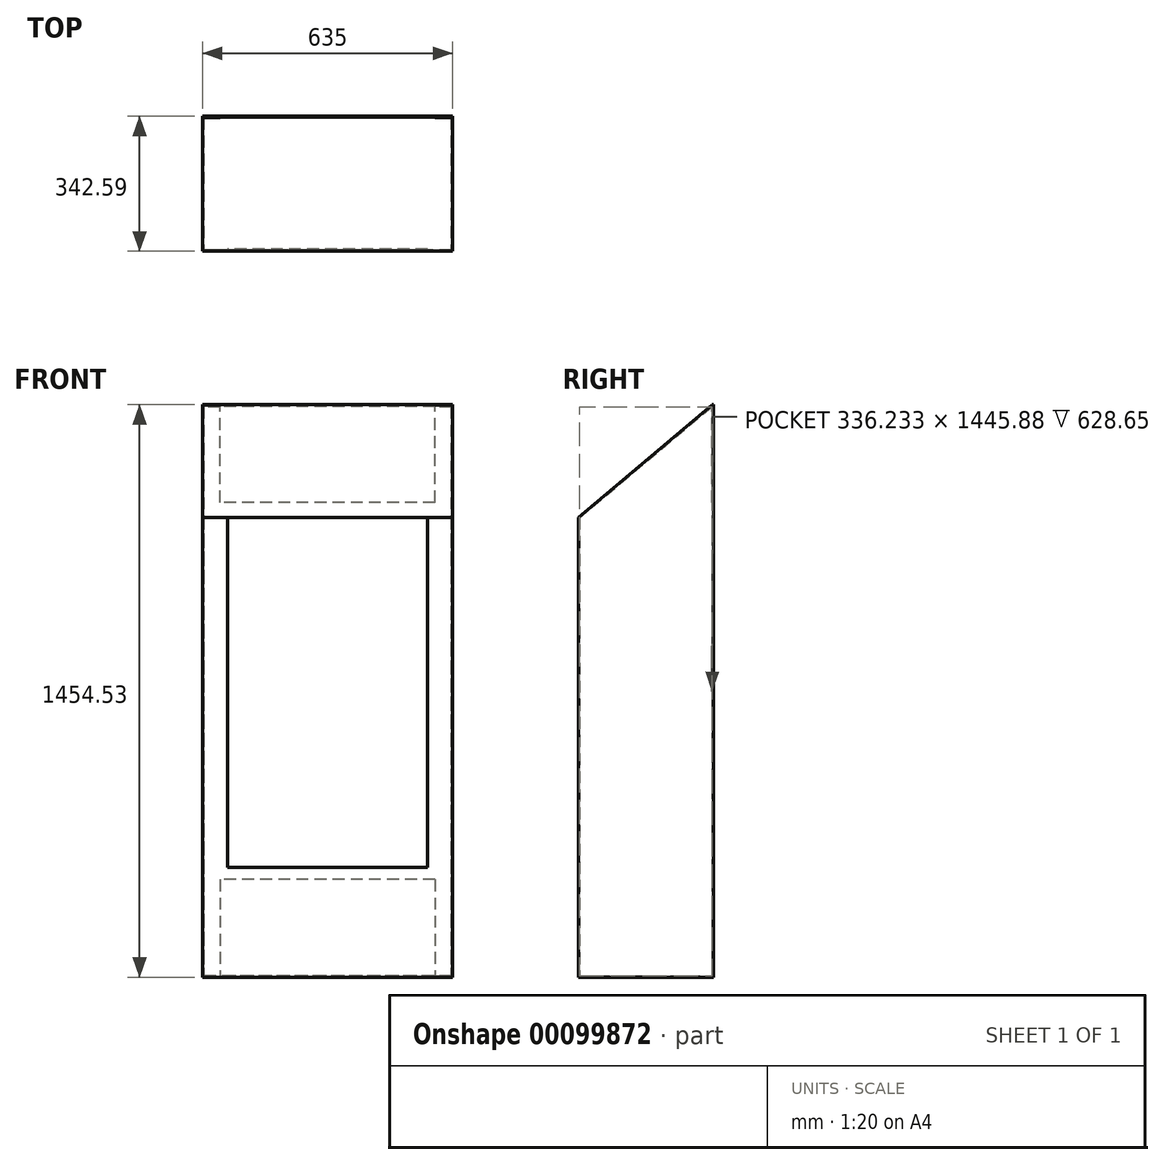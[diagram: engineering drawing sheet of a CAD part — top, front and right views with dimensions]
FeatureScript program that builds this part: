
annotation { "Feature Type Name" : "Feature", "Feature Type Description" : "" }
export const myFeature = defineFeature(function(context is Context, id is Id, definition is map)
    precondition{}
    {
        {
            var Q0;
            Q0=qCreatedBy(makeId("Right.planeOp"),FACE);
            var sketch = newSketch(context, id + "F0", { "sketchPlane" : qUnion([Q0])});
            skLineSegment(sketch, "E0", {"start": v(0, 0) * mm, "end": v(0, 1454.53) * mm});
            skLineSegment(sketch, "E1", {"start": v(0, 1454.53) * mm, "end": v(-341, 1168.4) * mm});
            skLineSegment(sketch, "E2", {"start": v(-341, 1168.4) * mm, "end": v(-341, 0) * mm});
            skLineSegment(sketch, "E3", {"start": v(-341, 0) * mm, "end": v(0, 0) * mm});
            skSolve(sketch);
        }
        {
            var Q0;
            Q0 = qSketchRegion(id + "F0", true);
            extrude(context, id + "F1", {"entities" : qUnion([Q0]), "endBound" : BoundingType.SYMMETRIC, "depth" : 635 * mm});
        }
        {
            var Q0;
            Q0=makeQuery(id+"F1.opExtrude","SWEPT_FACE",FACE,{"disambiguationData":[OSD([sQuery(id+"F0.wireOp",EDGE,"E0")])]});
            shell(context, id + "F2", {"entities" : qUnion([Q0]), "thickness" : 3.17 * mm});
        }
        {
            var Q0;
            Q0=qCreatedBy(makeId("Front.planeOp"),FACE);
            var sketch = newSketch(context, id + "F3", { "sketchPlane" : qUnion([Q0])});
            skLineSegment(sketch, "E4.bottom", {"start": v(273.11, 247.9) * mm, "end": v(-273.11, 247.9) * mm});
            skLineSegment(sketch, "E4.top", {"start": v(273.11, 1206.62) * mm, "end": v(-273.11, 1206.62) * mm});
            skLineSegment(sketch, "E4.left", {"start": v(317.5, 247.9) * mm, "end": v(317.5, 1206.62) * mm});
            skLineSegment(sketch, "E4.right", {"start": v(-317.5, 247.9) * mm, "end": v(-317.5, 1206.62) * mm});
            skLineSegment(sketch, "E5.top", {"start": v(317.5, 1454.53) * mm, "end": v(273.11, 1454.53) * mm});
            skLineSegment(sketch, "E5.left", {"start": v(317.5, 1206.62) * mm, "end": v(317.5, 1454.53) * mm});
            skLineSegment(sketch, "E5.right", {"start": v(273.11, 1206.62) * mm, "end": v(273.11, 1454.53) * mm});
            skLineSegment(sketch, "E6.top", {"start": v(-317.5, 1454.53) * mm, "end": v(-273.11, 1454.53) * mm});
            skLineSegment(sketch, "E6.left", {"start": v(-317.5, 1206.62) * mm, "end": v(-317.5, 1454.53) * mm});
            skLineSegment(sketch, "E6.right", {"start": v(-273.11, 1206.62) * mm, "end": v(-273.11, 1454.53) * mm});
            skLineSegment(sketch, "E7.top", {"start": v(-317.5, 0) * mm, "end": v(-273.11, 0) * mm});
            skLineSegment(sketch, "E7.left", {"start": v(-317.5, 247.9) * mm, "end": v(-317.5, 0) * mm});
            skLineSegment(sketch, "E7.right", {"start": v(-273.11, 247.9) * mm, "end": v(-273.11, 0) * mm});
            skLineSegment(sketch, "E8.top", {"start": v(317.5, 0) * mm, "end": v(273.11, 0) * mm});
            skLineSegment(sketch, "E8.left", {"start": v(317.5, 247.9) * mm, "end": v(317.5, 0) * mm});
            skLineSegment(sketch, "E8.right", {"start": v(273.11, 247.9) * mm, "end": v(273.11, 0) * mm});
            skSolve(sketch);
        }
        {
            var Q0;
            Q0 = qSketchRegion(id + "F3", true);
            extrude(context, id + "F4", {"entities" : qUnion([Q0]), "operationType" : NewBodyOperationType.ADD, "endBound" : BoundingType.SYMMETRIC, "depth" : 3.17 * mm});
        }
        {
            var Q0;
            Q0=makeQuery(id+"F1.opExtrude","SWEPT_FACE",FACE,{"disambiguationData":[OSD([sQuery(id+"F0.wireOp",EDGE,"E2")])]});
            var sketch = newSketch(context, id + "F5", { "sketchPlane" : qUnion([Q0])});
            skLineSegment(sketch, "E9.bottom", {"start": v(-254, 1168.4) * mm, "end": v(254, 1168.4) * mm});
            skLineSegment(sketch, "E9.top", {"start": v(-254, 279.4) * mm, "end": v(254, 279.4) * mm});
            skLineSegment(sketch, "E9.left", {"start": v(-254, 1168.4) * mm, "end": v(-254, 279.4) * mm});
            skLineSegment(sketch, "E9.right", {"start": v(254, 1168.4) * mm, "end": v(254, 279.4) * mm});
            skSolve(sketch);
        }
        {
            var Q0;
            Q0 = qSketchRegion(id + "F5", true);
            extrude(context, id + "F6", {"entities" : qUnion([Q0]), "operationType" : NewBodyOperationType.REMOVE, "endBound" : BoundingType.UP_TO_NEXT, "oppositeDirection" : true, "depth" : 25.4 * mm});
        }
    });
